# Revit family: 3-536-xx - Adelphi Vanity
name_source: partatom
category: Luminarias
units: mm (PartAtom-declared; Revit-internal decimal feet)

## family parameters
Anfitrión = Cara
Compartido = No
Corte con vacíos al cargar = No
Cota de conector redondo = Diámetro de uso
Origen de luz = Sí
Punto de cálculo de habitación = No
Tipo de pieza = Normal

## types (4) — shared parameters
Anchura rectángulo de emisión = 22 "
Archivo de red fotométrica = 3-537 Adelphi Vanity.ies
Cambio de temperatura de color de luz atenuada = <Ninguno>
Comentarios de vataje = 15.00W at 120 V
Fabricante = Oxygen - Lighting & Fans
Filtro de color = 16777215
Forma visible en renderización = No
Longitud de rectángulo de emisión = 1 "
Lámpara = LED Array
Main Diffuser = Matte White Acrylic
Modelo = 3-537-xx - 37-537-xx - Adelphi Vanity
URL = www.oxygenlighting.com
Voltage = 120 V
Ángulo de inclinación = 0.00°
zero-valued in all types: Elevación por defecto

## per-type parameters (varying)
| type | Metal Finish |
| 3-536-24 / Satin Nickel - Matte White Acrylic | 24 - Satin Nickel |
| 3-536-22 / Oiled Bronze - Matte White Acrylic | 22- Oiled Bronze |
| 3-536-40 / Aged Brass - Matte White Acrylic | 40 - Aged Brass |
| 3-536-15 / Black - Matte White Acrylic | 15 - Black |

## geometry (parser evidence)
native form markers: Sweep x4
no freeform markers — native parametric forms only
